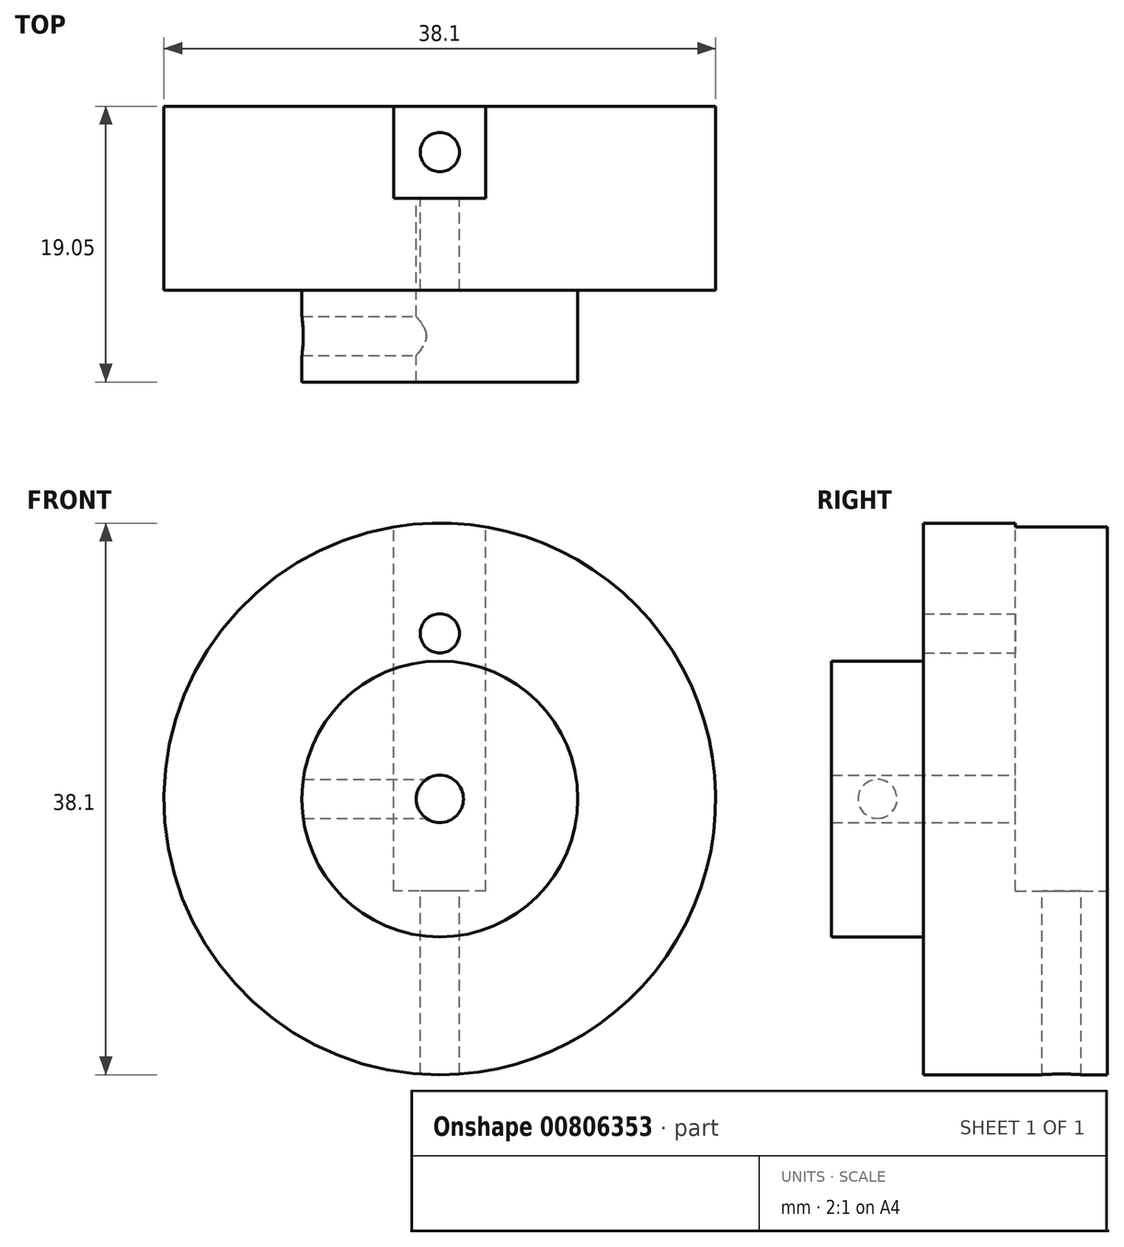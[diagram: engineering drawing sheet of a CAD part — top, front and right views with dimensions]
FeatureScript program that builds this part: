
annotation { "Feature Type Name" : "Feature", "Feature Type Description" : "" }
export const myFeature = defineFeature(function(context is Context, id is Id, definition is map)
    precondition{}
    {
        {
            var Q0;
            Q0=qCreatedBy(makeId("Front.planeOp"),FACE);
            var sketch = newSketch(context, id + "F0", { "sketchPlane" : qUnion([Q0])});
            skCircle(sketch, "E0", {"center": v(0, 0) * mm, "radius": 19.05 * mm});
            skCircle(sketch, "E1", {"center": v(0, 0) * mm, "radius": 9.53 * mm});
            skCircle(sketch, "E2", {"center": v(0, 0) * mm, "radius": 1.63 * mm});
            skLineSegment(sketch, "E3.bottom", {"start": v(3.18, -6.35) * mm, "end": v(-3.17, -6.35) * mm});
            skLineSegment(sketch, "E3.top", {"start": v(3.17, 19.75) * mm, "end": v(-3.18, 19.75) * mm});
            skLineSegment(sketch, "E3.left", {"start": v(3.18, -6.35) * mm, "end": v(3.17, 19.75) * mm});
            skLineSegment(sketch, "E3.right", {"start": v(-3.17, -6.35) * mm, "end": v(-3.18, 19.75) * mm});
            skSolve(sketch);
        }
        {
            var Q0;
            {var subQ0=sQuery(id+"F0.wireOp",EDGE,"E3.left");var subQ1=sQuery(id+"F0.wireOp",EDGE,"E0");var subQ2=makeQuery(id+"F0.imprint","INTERSECT",VERTEX,{"derivedFrom":[subQ1,subQ0]});Q0=makeQuery(id+"F0.imprint","IMPRINT",FACE,{"disambiguationData":[TD([[makeQuery(id+"F0.imprint","IMPRINT",EDGE,{"disambiguationData":[TD([[subQ2,1.0]])],"derivedFrom":subQ1}),1.0]])]});}
            var Q1;
            {var subQ0=sQuery(id+"F0.wireOp",EDGE,"E3.left");var subQ1=sQuery(id+"F0.wireOp",EDGE,"E0");var subQ2=makeQuery(id+"F0.imprint","INTERSECT",VERTEX,{"derivedFrom":[subQ1,subQ0]});Q1=makeQuery(id+"F0.imprint","IMPRINT",FACE,{"disambiguationData":[TD([[makeQuery(id+"F0.imprint","IMPRINT",EDGE,{"disambiguationData":[TD([[subQ2,-1.0]])],"derivedFrom":subQ1}),1.0]])]});}
            extrude(context, id + "F1", {"entities" : qUnion([Q0, Q1]), "depth" : 12.7 * mm, "offsetDistance" : 25.4 * mm});
        }
        {
            var Q0;
            Q0=makeQuery(id+"F0.imprint","IMPRINT",FACE,{"disambiguationData":[TD([[makeQuery(id+"F0.imprint","IMPRINT",EDGE,{"derivedFrom":sQuery(id+"F0.wireOp",EDGE,"E1")}),1.0]])]});
            var Q1;
            Q1=makeQuery(id+"F0.imprint","IMPRINT",FACE,{"disambiguationData":[TD([[makeQuery(id+"F0.imprint","IMPRINT",EDGE,{"derivedFrom":sQuery(id+"F0.wireOp",EDGE,"E2")}),-1.0]])]});
            extrude(context, id + "F2", {"entities" : qUnion([Q0, Q1]), "operationType" : NewBodyOperationType.ADD, "depth" : 19.05 * mm, "offsetDistance" : 25.4 * mm});
        }
        {
            var Q0;
            Q0=qCreatedBy(makeId("Right.planeOp"),FACE);
            var sketch = newSketch(context, id + "F3", { "sketchPlane" : qUnion([Q0])});
            skLineSegment(sketch, "E4", {"start": v(0, 0) * mm, "end": v(-19.05, 0) * mm, "construction": true});
            skCircle(sketch, "E5", {"center": v(-15.88, 0) * mm, "radius": 1.35 * mm});
            skSolve(sketch);
        }
        {
            var Q0;
            Q0 = qSketchRegion(id + "F3", true);
            extrude(context, id + "F4", {"entities" : qUnion([Q0]), "operationType" : NewBodyOperationType.REMOVE, "oppositeDirection" : true, "depth" : 25.4 * mm, "offsetDistance" : 25.4 * mm});
        }
        {
            var Q0;
            {var subQ5=sQuery(id+"F0.wireOp",EDGE,"E3.top");Q0=makeQuery(id+"F0.imprint","IMPRINT",FACE,{"disambiguationData":[TD([[makeQuery(id+"F0.imprint","IMPRINT",EDGE,{"derivedFrom":subQ5}),1.0]])]});}
            var Q1;
            {var subQ0=sQuery(id+"F0.wireOp",EDGE,"E3.left");var subQ1=sQuery(id+"F0.wireOp",EDGE,"E0");var subQ2=makeQuery(id+"F0.imprint","INTERSECT",VERTEX,{"derivedFrom":[subQ1,subQ0]});Q1=makeQuery(id+"F0.imprint","IMPRINT",FACE,{"disambiguationData":[TD([[makeQuery(id+"F0.imprint","IMPRINT",EDGE,{"disambiguationData":[TD([[subQ2,-1.0]])],"derivedFrom":subQ1}),1.0]])]});}
            var Q2;
            Q2=makeQuery(id+"F0.imprint","IMPRINT",FACE,{"disambiguationData":[TD([[makeQuery(id+"F0.imprint","IMPRINT",EDGE,{"derivedFrom":sQuery(id+"F0.wireOp",EDGE,"E2")}),-1.0]])]});
            extrude(context, id + "F5", {"entities" : qUnion([Q0, Q1, Q2]), "operationType" : NewBodyOperationType.REMOVE, "depth" : 6.35 * mm, "offsetDistance" : 25.4 * mm});
        }
        {
            var Q0;
            Q0=makeQuery(id+"F5.boolean.opBoolean","COPY",FACE,{"derivedFrom":makeQuery(id+"F5.opExtrude","CAP_FACE",FACE,{"disambiguationData":[OSD([sQuery(id+"F0.wireOp",EDGE,"E2"),sQuery(id+"F0.wireOp",EDGE,"E3.bottom"),sQuery(id+"F0.wireOp",EDGE,"E3.top"),sQuery(id+"F0.wireOp",EDGE,"E3.left"),sQuery(id+"F0.wireOp",EDGE,"E3.right")])],"isStart":false})});
            var sketch = newSketch(context, id + "F6", { "sketchPlane" : qUnion([Q0])});
            skCircle(sketch, "E6", {"center": v(0, 11.43) * mm, "radius": 1.35 * mm});
            skSolve(sketch);
        }
        {
            var Q0;
            Q0 = qSketchRegion(id + "F6", true);
            extrude(context, id + "F7", {"entities" : qUnion([Q0]), "operationType" : NewBodyOperationType.REMOVE, "oppositeDirection" : true, "depth" : 25.4 * mm, "offsetDistance" : 25.4 * mm});
        }
        {
            var Q0;
            Q0=makeQuery(id+"F5.boolean.opBoolean","COPY",FACE,{"derivedFrom":makeQuery(id+"F5.opExtrude","SWEPT_FACE",FACE,{"disambiguationData":[OSD([sQuery(id+"F0.wireOp",EDGE,"E3.bottom")])]})});
            var sketch = newSketch(context, id + "F8", { "sketchPlane" : qUnion([Q0])});
            skCircle(sketch, "E7", {"center": v(0, -3.18) * mm, "radius": 1.35 * mm});
            skSolve(sketch);
        }
        {
            var Q0;
            Q0 = qSketchRegion(id + "F8", true);
            extrude(context, id + "F9", {"entities" : qUnion([Q0]), "operationType" : NewBodyOperationType.REMOVE, "endBound" : BoundingType.THROUGH_ALL, "oppositeDirection" : true, "depth" : 25.4 * mm, "offsetDistance" : 25.4 * mm});
        }
    });
